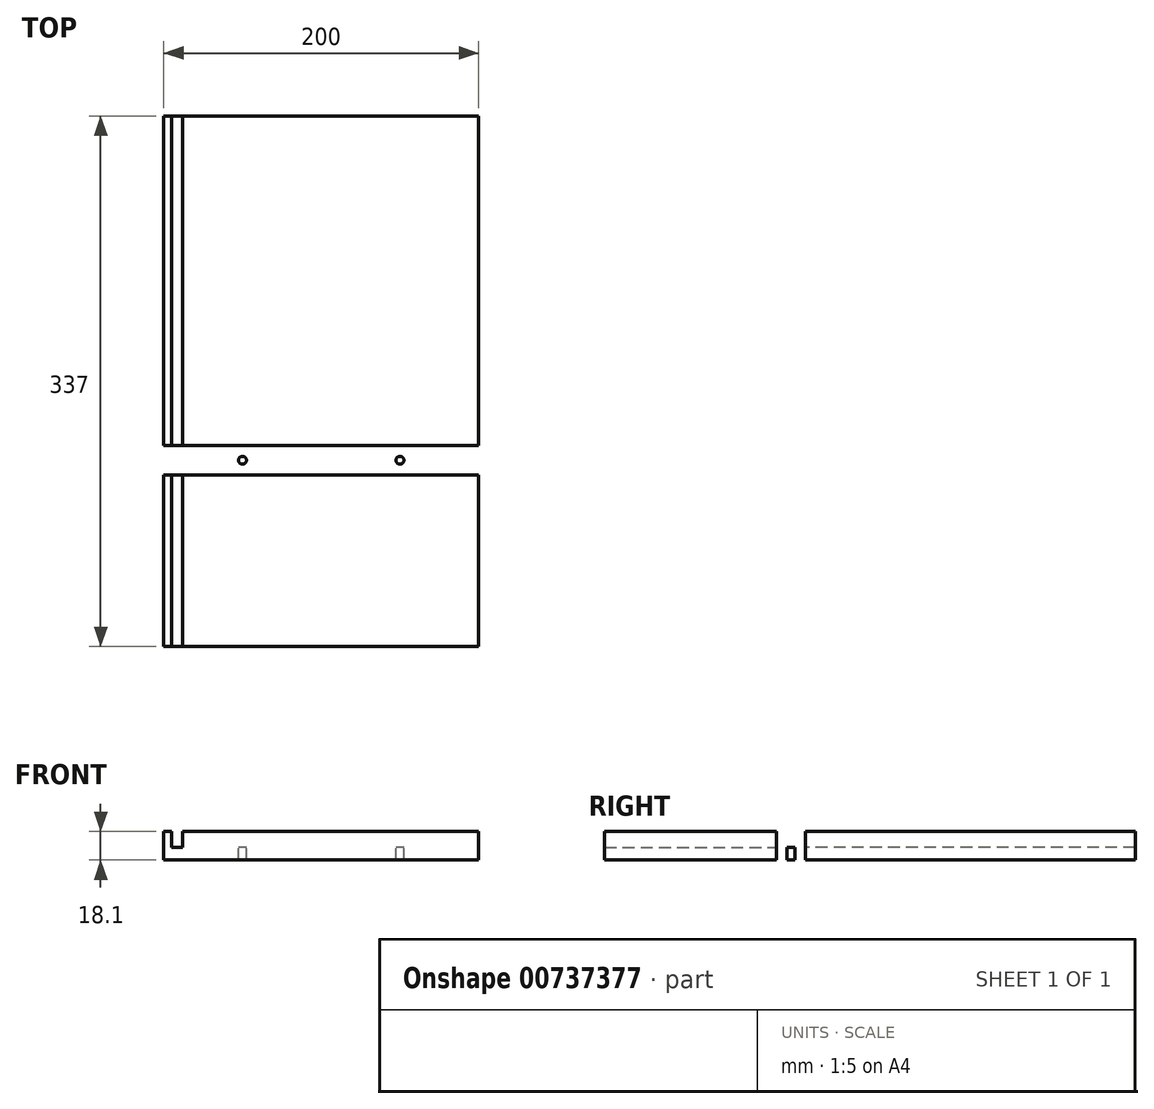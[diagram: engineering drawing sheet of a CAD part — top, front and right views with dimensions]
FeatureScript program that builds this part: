
annotation { "Feature Type Name" : "Feature", "Feature Type Description" : "" }
export const myFeature = defineFeature(function(context is Context, id is Id, definition is map)
    precondition{}
    {
        {
            var Q0;
            Q0=qCreatedBy(makeId("Top.planeOp"),FACE);
            var sketch = newSketch(context, id + "F0", { "sketchPlane" : qUnion([Q0])});
            skLineSegment(sketch, "E0.bottom", {"start": v(100, 168.5) * mm, "end": v(-100, 168.5) * mm});
            skLineSegment(sketch, "E0.top", {"start": v(100, -168.5) * mm, "end": v(-100, -168.5) * mm});
            skLineSegment(sketch, "E0.left", {"start": v(100, 168.5) * mm, "end": v(100, -168.5) * mm});
            skLineSegment(sketch, "E0.right", {"start": v(-100, 168.5) * mm, "end": v(-100, -168.5) * mm});
            skPoint(sketch, "E0.middle", {"position": v(0, 0) * mm});
            skSolve(sketch);
        }
        {
            var Q0;
            Q0=makeQuery(id+"F0.imprint","IMPRINT",FACE,{"disambiguationData":[TD([[makeQuery(id+"F0.imprint","IMPRINT",EDGE,{"derivedFrom":sQuery(id+"F0.wireOp",EDGE,"E0.bottom")}),1.0]])]});
            extrude(context, id + "F1", {"entities" : qUnion([Q0]), "depth" : 18.1 * mm, "offsetDistance" : 25 * mm});
        }
        {
            var Q0;
            Q0=makeQuery(id+"F1.opExtrude","CAP_FACE",FACE,{"disambiguationData":[OSD([sQuery(id+"F0.wireOp",EDGE,"E0.bottom"),sQuery(id+"F0.wireOp",EDGE,"E0.top"),sQuery(id+"F0.wireOp",EDGE,"E0.left"),sQuery(id+"F0.wireOp",EDGE,"E0.right")])],"isStart":false});
            var sketch = newSketch(context, id + "F2", { "sketchPlane" : qUnion([Q0])});
            skLineSegment(sketch, "E1", {"start": v(-100, -168.5) * mm, "end": v(-100, -59.5) * mm});
            skLineSegment(sketch, "E2", {"start": v(-100, -59.5) * mm, "end": v(100, -59.5) * mm});
            skLineSegment(sketch, "E3", {"start": v(100, -59.5) * mm, "end": v(100, -40.9) * mm});
            skLineSegment(sketch, "E4", {"start": v(100, -40.9) * mm, "end": v(-100, -40.9) * mm});
            skLineSegment(sketch, "E5", {"start": v(-100, -40.9) * mm, "end": v(-100, -59.5) * mm});
            skLineSegment(sketch, "E6.1.0.0", {"start": v(-75, -168.5) * mm, "end": v(-75, -59.5) * mm});
            skLineSegment(sketch, "E6.1.0.1", {"start": v(-75, -59.5) * mm, "end": v(125, -59.5) * mm});
            skLineSegment(sketch, "E6.1.0.2", {"start": v(125, -59.5) * mm, "end": v(125, -40.9) * mm});
            skLineSegment(sketch, "E6.1.0.3", {"start": v(125, -40.9) * mm, "end": v(-75, -40.9) * mm});
            skLineSegment(sketch, "E6.1.0.4", {"start": v(-75, -40.9) * mm, "end": v(-75, -59.5) * mm});
            skLineSegment(sketch, "E6.2.0.0", {"start": v(-50, -168.5) * mm, "end": v(-50, -59.5) * mm});
            skLineSegment(sketch, "E6.2.0.1", {"start": v(-50, -59.5) * mm, "end": v(150, -59.5) * mm});
            skLineSegment(sketch, "E6.2.0.2", {"start": v(150, -59.5) * mm, "end": v(150, -40.9) * mm});
            skLineSegment(sketch, "E6.2.0.3", {"start": v(150, -40.9) * mm, "end": v(-50, -40.9) * mm});
            skLineSegment(sketch, "E6.2.0.4", {"start": v(-50, -40.9) * mm, "end": v(-50, -59.5) * mm});
            skLineSegment(sketch, "E6.direction1", {"start": v(-100, -168.5) * mm, "end": v(-75, -168.5) * mm, "construction": true});
            skLineSegment(sketch, "E7", {"start": v(-100, 168.5) * mm, "end": v(-100, 158.5) * mm});
            skLineSegment(sketch, "E8", {"start": v(-100, 158.5) * mm, "end": v(-100, 139.9) * mm});
            skPoint(sketch, "E9.end.orphan", {"position": v(100, 158.5) * mm});
            skSolve(sketch);
        }
        {
            var Q0;
            Q0 = qSketchRegion(id + "F2", true);
            extrude(context, id + "F3", {"entities" : qUnion([Q0]), "operationType" : NewBodyOperationType.REMOVE, "oppositeDirection" : true, "depth" : 10 * mm, "offsetDistance" : 25 * mm});
        }
        {
            var Q0;
            Q0=makeQuery(id+"F3.boolean.opBoolean","COPY",FACE,{"derivedFrom":makeQuery(id+"F3.opExtrude","CAP_FACE",FACE,{"disambiguationData":[OSD([sQuery(id+"F2.wireOp",EDGE,"E2"),sQuery(id+"F2.wireOp",EDGE,"E4"),sQuery(id+"F2.wireOp",EDGE,"E5"),sQuery(id+"F2.wireOp",EDGE,"E6.1.0.1"),sQuery(id+"F2.wireOp",EDGE,"E6.1.0.3"),sQuery(id+"F2.wireOp",EDGE,"E6.2.0.1"),sQuery(id+"F2.wireOp",EDGE,"E6.2.0.2"),sQuery(id+"F2.wireOp",EDGE,"E6.2.0.3")])],"isStart":false})});
            var sketch = newSketch(context, id + "F4", { "sketchPlane" : qUnion([Q0])});
            skLineSegment(sketch, "E10", {"start": v(-100, -50.2) * mm, "end": v(100, -50.2) * mm});
            skLineSegment(sketch, "E11", {"start": v(100, -50.2) * mm, "end": v(50, -50.2) * mm});
            skLineSegment(sketch, "E12", {"start": v(-100, -50.2) * mm, "end": v(-50, -50.2) * mm});
            skCircle(sketch, "E13", {"center": v(-50, -50.2) * mm, "radius": 2.5 * mm});
            skCircle(sketch, "E14", {"center": v(50, -50.2) * mm, "radius": 2.5 * mm});
            skSolve(sketch);
        }
        {
            var Q0;
            {var subQ0=sQuery(id+"F4.wireOp",EDGE,"E12");var subQ1=sQuery(id+"F4.wireOp",EDGE,"E10");var subQ2=makeQuery(id+"F4.imprint","INTERSECT",VERTEX,{"derivedFrom":[subQ1,subQ0]});Q0=makeQuery(id+"F4.imprint","IMPRINT",FACE,{"disambiguationData":[TD([[makeQuery(id+"F4.imprint","IMPRINT",EDGE,{"disambiguationData":[TD([[subQ2,-1.0]])],"derivedFrom":subQ1}),1.0]])]});}
            var Q1;
            {var subQ0=sQuery(id+"F4.wireOp",EDGE,"E12");var subQ1=sQuery(id+"F4.wireOp",EDGE,"E10");var subQ2=makeQuery(id+"F4.imprint","INTERSECT",VERTEX,{"derivedFrom":[subQ1,subQ0]});Q1=makeQuery(id+"F4.imprint","IMPRINT",FACE,{"disambiguationData":[TD([[makeQuery(id+"F4.imprint","IMPRINT",EDGE,{"disambiguationData":[TD([[subQ2,-1.0]])],"derivedFrom":subQ1}),-1.0]])]});}
            var Q2;
            {var subQ0=sQuery(id+"F4.wireOp",EDGE,"E11");var subQ1=sQuery(id+"F4.wireOp",EDGE,"E10");var subQ2=makeQuery(id+"F4.imprint","INTERSECT",VERTEX,{"derivedFrom":[subQ1,subQ0]});Q2=makeQuery(id+"F4.imprint","IMPRINT",FACE,{"disambiguationData":[TD([[makeQuery(id+"F4.imprint","IMPRINT",EDGE,{"disambiguationData":[TD([[subQ2,1.0]])],"derivedFrom":subQ1}),1.0]])]});}
            var Q3;
            {var subQ0=sQuery(id+"F4.wireOp",EDGE,"E11");var subQ1=sQuery(id+"F4.wireOp",EDGE,"E10");var subQ2=makeQuery(id+"F4.imprint","INTERSECT",VERTEX,{"derivedFrom":[subQ1,subQ0]});Q3=makeQuery(id+"F4.imprint","IMPRINT",FACE,{"disambiguationData":[TD([[makeQuery(id+"F4.imprint","IMPRINT",EDGE,{"disambiguationData":[TD([[subQ2,1.0]])],"derivedFrom":subQ1}),-1.0]])]});}
            extrude(context, id + "F5", {"entities" : qUnion([Q0, Q1, Q2, Q3]), "operationType" : NewBodyOperationType.REMOVE, "oppositeDirection" : true, "depth" : 25 * mm, "offsetDistance" : 25 * mm});
        }
        {
            var Q0;
            {var subQ0=sQuery(id+"F0.wireOp",EDGE,"E0.bottom");var subQ1=sQuery(id+"F0.wireOp",EDGE,"E0.right");var subQ2=sQuery(id+"F0.wireOp",EDGE,"E0.left");Q0=makeQuery(id+"F3.boolean.opBoolean","SPLIT",FACE,{"disambiguationData":[TD([makeQuery(id+"F1.opExtrude","SWEPT_FACE",FACE,{"disambiguationData":[OSD([subQ0])]})])],"derivedFrom":makeQuery(id+"F1.opExtrude","CAP_FACE",FACE,{"disambiguationData":[OSD([subQ0,sQuery(id+"F0.wireOp",EDGE,"E0.top"),subQ2,subQ1])],"isStart":false})});}
            var sketch = newSketch(context, id + "F6", { "sketchPlane" : qUnion([Q0])});
            skLineSegment(sketch, "E15", {"start": v(-100, 168.5) * mm, "end": v(-95, 168.5) * mm});
            skLineSegment(sketch, "E16", {"start": v(-95, 168.5) * mm, "end": v(-95, -40.9) * mm});
            skLineSegment(sketch, "E17", {"start": v(-95, -40.9) * mm, "end": v(-88, -40.9) * mm});
            skLineSegment(sketch, "E18", {"start": v(-88, -40.9) * mm, "end": v(-88, 168.5) * mm});
            skSolve(sketch);
        }
        {
            var Q0;
            {var subQ0=sQuery(id+"F6.wireOp",EDGE,"E16");Q0=makeQuery(id+"F6.imprint","IMPRINT",FACE,{"disambiguationData":[TD([[makeQuery(id+"F6.imprint","IMPRINT",EDGE,{"derivedFrom":subQ0}),1.0]])]});}
            extrude(context, id + "F7", {"entities" : qUnion([Q0]), "operationType" : NewBodyOperationType.REMOVE, "oppositeDirection" : true, "depth" : 10 * mm, "offsetDistance" : 25 * mm});
        }
        {
            var Q0;
            {var subQ0=sQuery(id+"F0.wireOp",EDGE,"E0.top");var subQ1=sQuery(id+"F0.wireOp",EDGE,"E0.left");var subQ2=sQuery(id+"F0.wireOp",EDGE,"E0.right");Q0=makeQuery(id+"F3.boolean.opBoolean","SPLIT",FACE,{"disambiguationData":[TD([makeQuery(id+"F1.opExtrude","SWEPT_FACE",FACE,{"disambiguationData":[OSD([subQ0])]})])],"derivedFrom":makeQuery(id+"F1.opExtrude","CAP_FACE",FACE,{"disambiguationData":[OSD([sQuery(id+"F0.wireOp",EDGE,"E0.bottom"),subQ0,subQ1,subQ2])],"isStart":false})});}
            var sketch = newSketch(context, id + "F8", { "sketchPlane" : qUnion([Q0])});
            skLineSegment(sketch, "E19", {"start": v(-100, -168.5) * mm, "end": v(-95, -168.5) * mm});
            skLineSegment(sketch, "E20", {"start": v(-95, -168.5) * mm, "end": v(-95, -59.5) * mm});
            skLineSegment(sketch, "E21", {"start": v(-95, -59.5) * mm, "end": v(-88, -59.5) * mm});
            skLineSegment(sketch, "E22", {"start": v(-88, -59.5) * mm, "end": v(-88, -168.5) * mm});
            skSolve(sketch);
        }
        {
            var Q0;
            {var subQ0=sQuery(id+"F8.wireOp",EDGE,"E20");Q0=makeQuery(id+"F8.imprint","IMPRINT",FACE,{"disambiguationData":[TD([[makeQuery(id+"F8.imprint","IMPRINT",EDGE,{"derivedFrom":subQ0}),-1.0]])]});}
            extrude(context, id + "F9", {"entities" : qUnion([Q0]), "operationType" : NewBodyOperationType.REMOVE, "oppositeDirection" : true, "depth" : 10 * mm, "offsetDistance" : 25 * mm});
        }
    });
